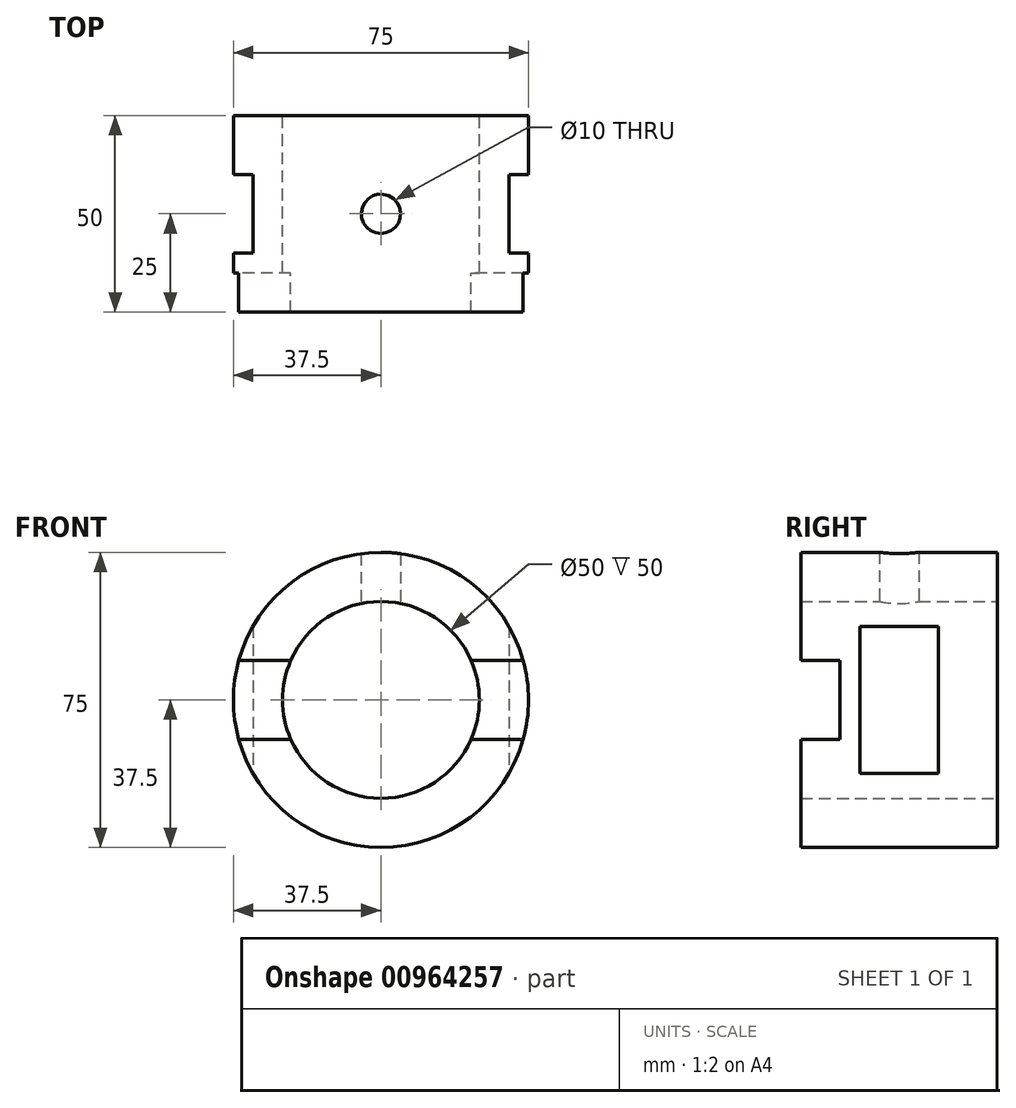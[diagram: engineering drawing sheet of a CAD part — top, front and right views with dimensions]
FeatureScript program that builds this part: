
annotation { "Feature Type Name" : "Feature", "Feature Type Description" : "" }
export const myFeature = defineFeature(function(context is Context, id is Id, definition is map)
    precondition{}
    {
        {
            var Q0;
            Q0=qCreatedBy(makeId("Front.planeOp"),FACE);
            var sketch = newSketch(context, id + "F0", { "sketchPlane" : qUnion([Q0])});
            skCircle(sketch, "E0", {"center": v(0, 0) * mm, "radius": 37.5 * mm});
            skCircle(sketch, "E1", {"center": v(0, 0) * mm, "radius": 25 * mm});
            skSolve(sketch);
        }
        {
            var Q0;
            Q0=makeQuery(id+"F0.imprint","IMPRINT",FACE,{"disambiguationData":[TD([[makeQuery(id+"F0.imprint","IMPRINT",EDGE,{"derivedFrom":sQuery(id+"F0.wireOp",EDGE,"E0")}),1.0]])]});
            extrude(context, id + "F1", {"entities" : qUnion([Q0]), "endBound" : BoundingType.SYMMETRIC, "depth" : 50 * mm, "offsetDistance" : 25 * mm});
        }
        {
            var Q0;
            Q0=qCreatedBy(makeId("Top.planeOp"),FACE);
            var sketch = newSketch(context, id + "F2", { "sketchPlane" : qUnion([Q0])});
            skCircle(sketch, "E2", {"center": v(0, 0) * mm, "radius": 5 * mm});
            skLineSegment(sketch, "E3.bottom", {"start": v(32.5, -10) * mm, "end": v(42.5, -10) * mm});
            skLineSegment(sketch, "E3.top", {"start": v(32.5, 10) * mm, "end": v(42.5, 10) * mm});
            skLineSegment(sketch, "E3.left", {"start": v(32.5, -10) * mm, "end": v(32.5, 10) * mm});
            skLineSegment(sketch, "E3.right", {"start": v(42.5, -10) * mm, "end": v(42.5, 10) * mm});
            skPoint(sketch, "E3.middle", {"position": v(37.5, 0) * mm});
            skLineSegment(sketch, "E4", {"start": v(0, 0) * mm, "end": v(0, 43.25) * mm, "construction": true});
            skLineSegment(sketch, "E5", {"start": v(0, 43.25) * mm, "end": v(0, -33.2) * mm, "construction": true});
            skLineSegment(sketch, "E6.MirrorCS", {"start": v(-42.5, -10) * mm, "end": v(-42.5, 10) * mm});
            skLineSegment(sketch, "E7.MirrorCS", {"start": v(-32.5, 10) * mm, "end": v(-42.5, 10) * mm});
            skLineSegment(sketch, "E8.MirrorCS", {"start": v(-32.5, -10) * mm, "end": v(-42.5, -10) * mm});
            skPoint(sketch, "E9.MirrorP", {"position": v(-37.5, 0) * mm});
            skLineSegment(sketch, "E10.MirrorCS", {"start": v(-32.5, -10) * mm, "end": v(-32.5, 10) * mm});
            skLineSegment(sketch, "E11", {"start": v(-37.5, -25) * mm, "end": v(-37.5, 25) * mm});
            skLineSegment(sketch, "E12", {"start": v(37.5, 25) * mm, "end": v(37.5, -25) * mm});
            skLineSegment(sketch, "E13.0", {"start": v(37.5, -25) * mm, "end": v(-37.5, -25) * mm});
            skLineSegment(sketch, "E14.bottom", {"start": v(37.5, -35) * mm, "end": v(-37.5, -35) * mm});
            skLineSegment(sketch, "E14.top", {"start": v(37.5, -15) * mm, "end": v(-37.5, -15) * mm});
            skLineSegment(sketch, "E14.left", {"start": v(37.5, -35) * mm, "end": v(37.5, -15) * mm});
            skLineSegment(sketch, "E14.right", {"start": v(-37.5, -35) * mm, "end": v(-37.5, -15) * mm});
            skPoint(sketch, "E14.middle", {"position": v(0, -25) * mm});
            skSolve(sketch);
        }
        {
            var Q0;
            {var subQ0=sQuery(id+"F2.wireOp",EDGE,"E10.MirrorCS");Q0=makeQuery(id+"F2.imprint","IMPRINT",FACE,{"disambiguationData":[TD([[makeQuery(id+"F2.imprint","IMPRINT",EDGE,{"derivedFrom":subQ0}),1.0]])]});}
            var Q1;
            {var subQ0=sQuery(id+"F2.wireOp",EDGE,"E3.left");Q1=makeQuery(id+"F2.imprint","IMPRINT",FACE,{"disambiguationData":[TD([[makeQuery(id+"F2.imprint","IMPRINT",EDGE,{"derivedFrom":subQ0}),-1.0]])]});}
            extrude(context, id + "F3", {"entities" : qUnion([Q0, Q1]), "operationType" : NewBodyOperationType.REMOVE, "endBound" : BoundingType.SYMMETRIC, "depth" : 100 * mm, "offsetDistance" : 25 * mm});
        }
        {
            var Q0;
            {var subQ0=sQuery(id+"F2.wireOp",EDGE,"E13.0");Q0=makeQuery(id+"F2.imprint","IMPRINT",FACE,{"disambiguationData":[TD([[makeQuery(id+"F2.imprint","IMPRINT",EDGE,{"derivedFrom":subQ0}),-1.0]])]});}
            extrude(context, id + "F4", {"entities" : qUnion([Q0]), "operationType" : NewBodyOperationType.REMOVE, "endBound" : BoundingType.SYMMETRIC, "depth" : 20 * mm, "offsetDistance" : 25 * mm});
        }
        {
            var Q0;
            {var subQ0=sQuery(id+"F2.wireOp",EDGE,"E13.0");Q0=makeQuery(id+"F2.imprint","IMPRINT",FACE,{"disambiguationData":[TD([[makeQuery(id+"F2.imprint","IMPRINT",EDGE,{"derivedFrom":subQ0}),-1.0]])]});}
            extrude(context, id + "F5", {"entities" : qUnion([Q0]), "operationType" : NewBodyOperationType.REMOVE, "endBound" : BoundingType.SYMMETRIC, "oppositeDirection" : true, "depth" : 20 * mm, "offsetDistance" : 25 * mm});
        }
        {
            var Q0;
            Q0=makeQuery(id+"F2.imprint","IMPRINT",FACE,{"disambiguationData":[TD([[makeQuery(id+"F2.imprint","IMPRINT",EDGE,{"derivedFrom":sQuery(id+"F2.wireOp",EDGE,"E2")}),1.0]])]});
            var Q1;
            Q1=sQuery(id+"F2.wireOp",EDGE,"E2");
            extrude(context, id + "F6", {"entities" : qUnion([Q0]), "operationType" : NewBodyOperationType.REMOVE, "surfaceEntities" : qUnion([Q1]), "endBound" : BoundingType.THROUGH_ALL, "depth" : 25 * mm, "offsetDistance" : 25 * mm});
        }
    });
